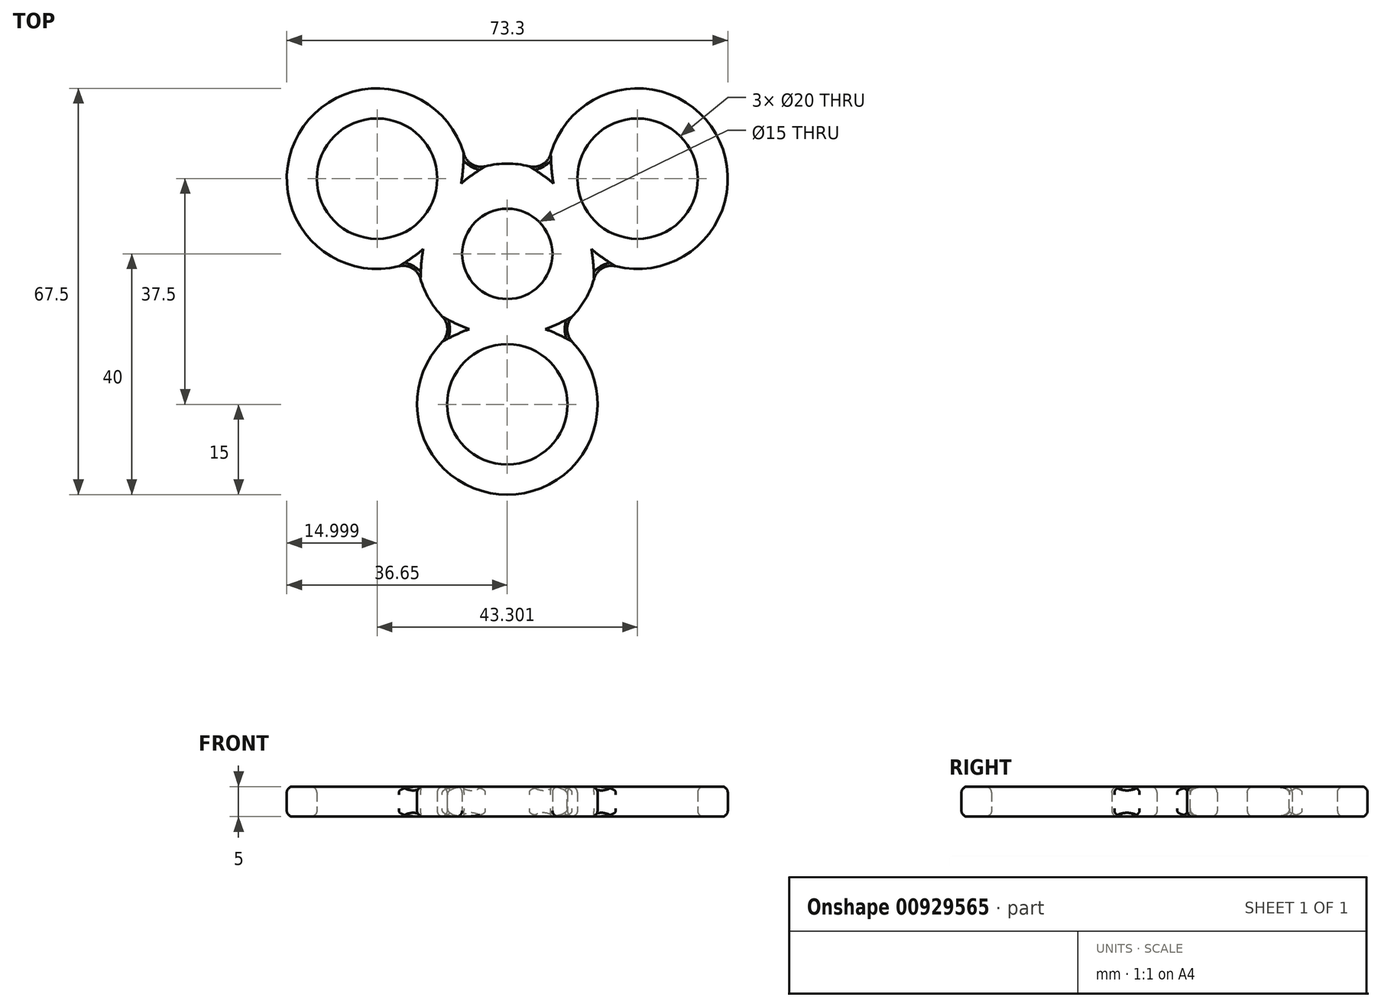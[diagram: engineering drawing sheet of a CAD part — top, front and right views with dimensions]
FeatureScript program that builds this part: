
annotation { "Feature Type Name" : "Feature", "Feature Type Description" : "" }
export const myFeature = defineFeature(function(context is Context, id is Id, definition is map)
    precondition{}
    {
        {
            var Q0;
            Q0=qCreatedBy(makeId("Top.planeOp"),FACE);
            var sketch = newSketch(context, id + "F0", { "sketchPlane" : qUnion([Q0])});
            skCircle(sketch, "E0", {"center": v(0, 0) * mm, "radius": 7.5 * mm});
            skCircle(sketch, "E1", {"center": v(0, 0) * mm, "radius": 15 * mm});
            skCircle(sketch, "E2", {"center": v(0, 0) * mm, "radius": 25 * mm, "construction": true});
            skLineSegment(sketch, "E3", {"start": v(0, 0) * mm, "end": v(0, -25) * mm, "construction": true});
            skCircle(sketch, "E4", {"center": v(0, -25) * mm, "radius": 15 * mm});
            skCircle(sketch, "E5", {"center": v(0, -25) * mm, "radius": 10 * mm});
            skCircle(sketch, "E6.1.0", {"center": v(21.65, 12.5) * mm, "radius": 15 * mm});
            skCircle(sketch, "E6.1.1", {"center": v(21.65, 12.5) * mm, "radius": 10 * mm});
            skCircle(sketch, "E6.2.0", {"center": v(-21.65, 12.5) * mm, "radius": 15 * mm});
            skCircle(sketch, "E6.2.1", {"center": v(-21.65, 12.5) * mm, "radius": 10 * mm});
            skSolve(sketch);
        }
        {
            var Q0;
            Q0 = qSketchRegion(id + "F0", true);
            extrude(context, id + "F1", {"entities" : qUnion([Q0]), "depth" : 5 * mm, "offsetDistance" : 25.4 * mm});
        }
        {
            var Q0;
            Q0=makeQuery(id+"F1.opExtrude","CAP_EDGE",EDGE,{"disambiguationData":[OSD([sQuery(id+"F0.wireOp",EDGE,"E6.2.0")])],"isStart":false});
            var Q1;
            Q1=makeQuery(id+"F1.opExtrude","CAP_EDGE",EDGE,{"disambiguationData":[OSD([sQuery(id+"F0.wireOp",EDGE,"E6.2.1")])],"isStart":false});
            var Q2;
            Q2=makeQuery(id+"F1.opExtrude","CAP_EDGE",EDGE,{"disambiguationData":[OSD([sQuery(id+"F0.wireOp",EDGE,"E6.2.1")])],"isStart":true});
            var Q3;
            Q3=makeQuery(id+"F1.opExtrude","CAP_EDGE",EDGE,{"disambiguationData":[OSD([sQuery(id+"F0.wireOp",EDGE,"E6.2.0")])],"isStart":true});
            var Q4;
            Q4=makeQuery(id+"F1.opExtrude","CAP_EDGE",EDGE,{"disambiguationData":[OSD([sQuery(id+"F0.wireOp",EDGE,"E0")])],"isStart":false});
            var Q5;
            Q5=makeQuery(id+"F1.opExtrude","CAP_EDGE",EDGE,{"disambiguationData":[OSD([sQuery(id+"F0.wireOp",EDGE,"E0")])],"isStart":true});
            var Q6;
            {var subQ0=sQuery(id+"F0.wireOp",EDGE,"E1");Q6=makeQuery(id+"F1.opExtrude","CAP_EDGE",EDGE,{"disambiguationData":[OSD([subQ0]),TDD([makeQuery(id+"F0.imprint","IMPRINT",EDGE,{"disambiguationData":[TD([[makeQuery(id+"F0.imprint","INTERSECT",VERTEX,{"disambiguationData":[OD(1.0)],"derivedFrom":[subQ0,sQuery(id+"F0.wireOp",EDGE,"E6.2.0")]}),-1.0]])],"derivedFrom":subQ0})])],"isStart":true});}
            var Q7;
            {var subQ0=sQuery(id+"F0.wireOp",EDGE,"E1");Q7=makeQuery(id+"F1.opExtrude","CAP_EDGE",EDGE,{"disambiguationData":[OSD([subQ0]),TDD([makeQuery(id+"F0.imprint","IMPRINT",EDGE,{"disambiguationData":[TD([[makeQuery(id+"F0.imprint","INTERSECT",VERTEX,{"disambiguationData":[OD(1.0)],"derivedFrom":[subQ0,sQuery(id+"F0.wireOp",EDGE,"E6.2.0")]}),-1.0]])],"derivedFrom":subQ0})])],"isStart":false});}
            var Q8;
            Q8=makeQuery(id+"F1.opExtrude","CAP_EDGE",EDGE,{"disambiguationData":[OSD([sQuery(id+"F0.wireOp",EDGE,"E4")])],"isStart":false});
            var Q9;
            Q9=makeQuery(id+"F1.opExtrude","CAP_EDGE",EDGE,{"disambiguationData":[OSD([sQuery(id+"F0.wireOp",EDGE,"E5")])],"isStart":false});
            var Q10;
            Q10=makeQuery(id+"F1.opExtrude","CAP_EDGE",EDGE,{"disambiguationData":[OSD([sQuery(id+"F0.wireOp",EDGE,"E5")])],"isStart":true});
            var Q11;
            Q11=makeQuery(id+"F1.opExtrude","CAP_EDGE",EDGE,{"disambiguationData":[OSD([sQuery(id+"F0.wireOp",EDGE,"E4")])],"isStart":true});
            var Q12;
            {var subQ0=sQuery(id+"F0.wireOp",EDGE,"E1");Q12=makeQuery(id+"F1.opExtrude","CAP_EDGE",EDGE,{"disambiguationData":[OSD([subQ0]),TDD([makeQuery(id+"F0.imprint","IMPRINT",EDGE,{"disambiguationData":[TD([[makeQuery(id+"F0.imprint","INTERSECT",VERTEX,{"disambiguationData":[OD(1.0)],"derivedFrom":[subQ0,sQuery(id+"F0.wireOp",EDGE,"E4")]}),-1.0]])],"derivedFrom":subQ0})])],"isStart":false});}
            var Q13;
            {var subQ0=sQuery(id+"F0.wireOp",EDGE,"E1");Q13=makeQuery(id+"F1.opExtrude","CAP_EDGE",EDGE,{"disambiguationData":[OSD([subQ0]),TDD([makeQuery(id+"F0.imprint","IMPRINT",EDGE,{"disambiguationData":[TD([[makeQuery(id+"F0.imprint","INTERSECT",VERTEX,{"disambiguationData":[OD(1.0)],"derivedFrom":[subQ0,sQuery(id+"F0.wireOp",EDGE,"E4")]}),-1.0]])],"derivedFrom":subQ0})])],"isStart":true});}
            var Q14;
            {var subQ0=sQuery(id+"F0.wireOp",EDGE,"E1");Q14=makeQuery(id+"F1.opExtrude","CAP_EDGE",EDGE,{"disambiguationData":[OSD([subQ0]),TDD([makeQuery(id+"F0.imprint","IMPRINT",EDGE,{"disambiguationData":[TD([[makeQuery(id+"F0.imprint","INTERSECT",VERTEX,{"disambiguationData":[OD(0.0)],"derivedFrom":[subQ0,sQuery(id+"F0.wireOp",EDGE,"E6.1.0")]}),-1.0]])],"derivedFrom":subQ0})])],"isStart":false});}
            var Q15;
            Q15=makeQuery(id+"F1.opExtrude","CAP_EDGE",EDGE,{"disambiguationData":[OSD([sQuery(id+"F0.wireOp",EDGE,"E6.1.1")])],"isStart":false});
            var Q16;
            Q16=makeQuery(id+"F1.opExtrude","CAP_EDGE",EDGE,{"disambiguationData":[OSD([sQuery(id+"F0.wireOp",EDGE,"E6.1.0")])],"isStart":false});
            var Q17;
            Q17=makeQuery(id+"F1.opExtrude","CAP_EDGE",EDGE,{"disambiguationData":[OSD([sQuery(id+"F0.wireOp",EDGE,"E6.1.1")])],"isStart":true});
            var Q18;
            Q18=makeQuery(id+"F1.opExtrude","CAP_EDGE",EDGE,{"disambiguationData":[OSD([sQuery(id+"F0.wireOp",EDGE,"E6.1.0")])],"isStart":true});
            var Q19;
            {var subQ0=sQuery(id+"F0.wireOp",EDGE,"E1");Q19=makeQuery(id+"F1.opExtrude","CAP_EDGE",EDGE,{"disambiguationData":[OSD([subQ0]),TDD([makeQuery(id+"F0.imprint","IMPRINT",EDGE,{"disambiguationData":[TD([[makeQuery(id+"F0.imprint","INTERSECT",VERTEX,{"disambiguationData":[OD(0.0)],"derivedFrom":[subQ0,sQuery(id+"F0.wireOp",EDGE,"E6.1.0")]}),-1.0]])],"derivedFrom":subQ0})])],"isStart":true});}
            fillet(context, id + "F2", {"entities" : qUnion([Q0, Q1, Q2, Q3, Q4, Q5, Q6, Q7, Q8, Q9, Q10, Q11, Q12, Q13, Q14, Q15, Q16, Q17, Q18, Q19]), "radius" : 1 * mm, "tangentPropagation" : true, "allowEdgeOverflow" : false});
        }
        {
            var Q0;
            {var subQ0=sQuery(id+"F0.wireOp",EDGE,"E4");var subQ1=sQuery(id+"F0.wireOp",EDGE,"E1");Q0=makeQuery(id+"F2.opFillet","BLEND_EDGE",EDGE,{"blendedFrom":[makeQuery(id+"F1.opExtrude","CAP_EDGE",EDGE,{"disambiguationData":[OSD([subQ1]),TDD([makeQuery(id+"F0.imprint","IMPRINT",EDGE,{"disambiguationData":[TD([[makeQuery(id+"F0.imprint","INTERSECT",VERTEX,{"disambiguationData":[OD(1.0)],"derivedFrom":[subQ1,subQ0]}),-1.0]])],"derivedFrom":subQ1})])],"isStart":false}),makeQuery(id+"F1.opExtrude","CAP_EDGE",EDGE,{"disambiguationData":[OSD([subQ0])],"isStart":false})],"blendedInto":[]});}
            var Q1;
            {var subQ0=sQuery(id+"F0.wireOp",EDGE,"E4");var subQ1=sQuery(id+"F0.wireOp",EDGE,"E1");Q1=makeQuery(id+"F2.opFillet","BLEND_EDGE",EDGE,{"blendedFrom":[makeQuery(id+"F1.opExtrude","CAP_EDGE",EDGE,{"disambiguationData":[OSD([subQ1]),TDD([makeQuery(id+"F0.imprint","IMPRINT",EDGE,{"disambiguationData":[TD([[makeQuery(id+"F0.imprint","INTERSECT",VERTEX,{"disambiguationData":[OD(1.0)],"derivedFrom":[subQ1,subQ0]}),-1.0]])],"derivedFrom":subQ1})])],"isStart":true}),makeQuery(id+"F1.opExtrude","CAP_EDGE",EDGE,{"disambiguationData":[OSD([subQ0])],"isStart":true})],"blendedInto":[]});}
            var Q2;
            {var subQ0=sQuery(id+"F0.wireOp",EDGE,"E4");var subQ1=sQuery(id+"F0.wireOp",EDGE,"E1");Q2=makeQuery(id+"F1.opExtrude","SWEPT_EDGE",EDGE,{"disambiguationData":[OSD([subQ1,subQ0]),TDD([makeQuery(id+"F0.imprint","INTERSECT",VERTEX,{"disambiguationData":[OD(1.0)],"derivedFrom":[subQ1,subQ0]})])]});}
            var Q3;
            {var subQ0=sQuery(id+"F0.wireOp",EDGE,"E6.1.0");var subQ1=sQuery(id+"F0.wireOp",EDGE,"E1");Q3=makeQuery(id+"F2.opFillet","BLEND_EDGE",EDGE,{"blendedFrom":[makeQuery(id+"F1.opExtrude","CAP_EDGE",EDGE,{"disambiguationData":[OSD([subQ1]),TDD([makeQuery(id+"F0.imprint","IMPRINT",EDGE,{"disambiguationData":[TD([[makeQuery(id+"F0.imprint","INTERSECT",VERTEX,{"disambiguationData":[OD(1.0)],"derivedFrom":[subQ1,sQuery(id+"F0.wireOp",EDGE,"E4")]}),-1.0]])],"derivedFrom":subQ1})])],"isStart":false}),makeQuery(id+"F1.opExtrude","CAP_EDGE",EDGE,{"disambiguationData":[OSD([subQ0])],"isStart":false})],"blendedInto":[]});}
            var Q4;
            {var subQ0=sQuery(id+"F0.wireOp",EDGE,"E6.1.0");var subQ1=sQuery(id+"F0.wireOp",EDGE,"E1");Q4=makeQuery(id+"F1.opExtrude","SWEPT_EDGE",EDGE,{"disambiguationData":[OSD([subQ1,subQ0]),TDD([makeQuery(id+"F0.imprint","INTERSECT",VERTEX,{"disambiguationData":[OD(1.0)],"derivedFrom":[subQ1,subQ0]})])]});}
            var Q5;
            {var subQ0=sQuery(id+"F0.wireOp",EDGE,"E6.1.0");var subQ1=sQuery(id+"F0.wireOp",EDGE,"E1");Q5=makeQuery(id+"F2.opFillet","BLEND_EDGE",EDGE,{"blendedFrom":[makeQuery(id+"F1.opExtrude","CAP_EDGE",EDGE,{"disambiguationData":[OSD([subQ1]),TDD([makeQuery(id+"F0.imprint","IMPRINT",EDGE,{"disambiguationData":[TD([[makeQuery(id+"F0.imprint","INTERSECT",VERTEX,{"disambiguationData":[OD(1.0)],"derivedFrom":[subQ1,sQuery(id+"F0.wireOp",EDGE,"E4")]}),-1.0]])],"derivedFrom":subQ1})])],"isStart":true}),makeQuery(id+"F1.opExtrude","CAP_EDGE",EDGE,{"disambiguationData":[OSD([subQ0])],"isStart":true})],"blendedInto":[]});}
            var Q6;
            {var subQ0=sQuery(id+"F0.wireOp",EDGE,"E6.1.0");var subQ1=sQuery(id+"F0.wireOp",EDGE,"E1");Q6=makeQuery(id+"F2.opFillet","BLEND_EDGE",EDGE,{"blendedFrom":[makeQuery(id+"F1.opExtrude","CAP_EDGE",EDGE,{"disambiguationData":[OSD([subQ1]),TDD([makeQuery(id+"F0.imprint","IMPRINT",EDGE,{"disambiguationData":[TD([[makeQuery(id+"F0.imprint","INTERSECT",VERTEX,{"disambiguationData":[OD(0.0)],"derivedFrom":[subQ1,subQ0]}),-1.0]])],"derivedFrom":subQ1})])],"isStart":false}),makeQuery(id+"F1.opExtrude","CAP_EDGE",EDGE,{"disambiguationData":[OSD([subQ0])],"isStart":false})],"blendedInto":[]});}
            var Q7;
            {var subQ0=sQuery(id+"F0.wireOp",EDGE,"E6.1.0");var subQ1=sQuery(id+"F0.wireOp",EDGE,"E1");Q7=makeQuery(id+"F1.opExtrude","SWEPT_EDGE",EDGE,{"disambiguationData":[OSD([subQ1,subQ0]),TDD([makeQuery(id+"F0.imprint","INTERSECT",VERTEX,{"disambiguationData":[OD(0.0)],"derivedFrom":[subQ1,subQ0]})])]});}
            var Q8;
            {var subQ0=sQuery(id+"F0.wireOp",EDGE,"E6.1.0");var subQ1=sQuery(id+"F0.wireOp",EDGE,"E1");Q8=makeQuery(id+"F2.opFillet","BLEND_EDGE",EDGE,{"blendedFrom":[makeQuery(id+"F1.opExtrude","CAP_EDGE",EDGE,{"disambiguationData":[OSD([subQ1]),TDD([makeQuery(id+"F0.imprint","IMPRINT",EDGE,{"disambiguationData":[TD([[makeQuery(id+"F0.imprint","INTERSECT",VERTEX,{"disambiguationData":[OD(0.0)],"derivedFrom":[subQ1,subQ0]}),-1.0]])],"derivedFrom":subQ1})])],"isStart":true}),makeQuery(id+"F1.opExtrude","CAP_EDGE",EDGE,{"disambiguationData":[OSD([subQ0])],"isStart":true})],"blendedInto":[]});}
            var Q9;
            {var subQ0=sQuery(id+"F0.wireOp",EDGE,"E6.2.0");var subQ1=sQuery(id+"F0.wireOp",EDGE,"E1");Q9=makeQuery(id+"F2.opFillet","BLEND_EDGE",EDGE,{"blendedFrom":[makeQuery(id+"F1.opExtrude","CAP_EDGE",EDGE,{"disambiguationData":[OSD([subQ1]),TDD([makeQuery(id+"F0.imprint","IMPRINT",EDGE,{"disambiguationData":[TD([[makeQuery(id+"F0.imprint","INTERSECT",VERTEX,{"disambiguationData":[OD(0.0)],"derivedFrom":[subQ1,sQuery(id+"F0.wireOp",EDGE,"E6.1.0")]}),-1.0]])],"derivedFrom":subQ1})])],"isStart":false}),makeQuery(id+"F1.opExtrude","CAP_EDGE",EDGE,{"disambiguationData":[OSD([subQ0])],"isStart":false})],"blendedInto":[]});}
            var Q10;
            {var subQ0=sQuery(id+"F0.wireOp",EDGE,"E6.2.0");var subQ1=sQuery(id+"F0.wireOp",EDGE,"E1");Q10=makeQuery(id+"F1.opExtrude","SWEPT_EDGE",EDGE,{"disambiguationData":[OSD([subQ1,subQ0]),TDD([makeQuery(id+"F0.imprint","INTERSECT",VERTEX,{"disambiguationData":[OD(0.0)],"derivedFrom":[subQ1,subQ0]})])]});}
            var Q11;
            {var subQ0=sQuery(id+"F0.wireOp",EDGE,"E6.2.0");var subQ1=sQuery(id+"F0.wireOp",EDGE,"E1");Q11=makeQuery(id+"F2.opFillet","BLEND_EDGE",EDGE,{"blendedFrom":[makeQuery(id+"F1.opExtrude","CAP_EDGE",EDGE,{"disambiguationData":[OSD([subQ1]),TDD([makeQuery(id+"F0.imprint","IMPRINT",EDGE,{"disambiguationData":[TD([[makeQuery(id+"F0.imprint","INTERSECT",VERTEX,{"disambiguationData":[OD(0.0)],"derivedFrom":[subQ1,sQuery(id+"F0.wireOp",EDGE,"E6.1.0")]}),-1.0]])],"derivedFrom":subQ1})])],"isStart":true}),makeQuery(id+"F1.opExtrude","CAP_EDGE",EDGE,{"disambiguationData":[OSD([subQ0])],"isStart":true})],"blendedInto":[]});}
            var Q12;
            {var subQ0=sQuery(id+"F0.wireOp",EDGE,"E6.2.0");var subQ1=sQuery(id+"F0.wireOp",EDGE,"E1");Q12=makeQuery(id+"F2.opFillet","BLEND_EDGE",EDGE,{"blendedFrom":[makeQuery(id+"F1.opExtrude","CAP_EDGE",EDGE,{"disambiguationData":[OSD([subQ1]),TDD([makeQuery(id+"F0.imprint","IMPRINT",EDGE,{"disambiguationData":[TD([[makeQuery(id+"F0.imprint","INTERSECT",VERTEX,{"disambiguationData":[OD(1.0)],"derivedFrom":[subQ1,subQ0]}),-1.0]])],"derivedFrom":subQ1})])],"isStart":false}),makeQuery(id+"F1.opExtrude","CAP_EDGE",EDGE,{"disambiguationData":[OSD([subQ0])],"isStart":false})],"blendedInto":[]});}
            var Q13;
            {var subQ0=sQuery(id+"F0.wireOp",EDGE,"E6.2.0");var subQ1=sQuery(id+"F0.wireOp",EDGE,"E1");Q13=makeQuery(id+"F1.opExtrude","SWEPT_EDGE",EDGE,{"disambiguationData":[OSD([subQ1,subQ0]),TDD([makeQuery(id+"F0.imprint","INTERSECT",VERTEX,{"disambiguationData":[OD(1.0)],"derivedFrom":[subQ1,subQ0]})])]});}
            var Q14;
            {var subQ0=sQuery(id+"F0.wireOp",EDGE,"E6.2.0");var subQ1=sQuery(id+"F0.wireOp",EDGE,"E1");Q14=makeQuery(id+"F2.opFillet","BLEND_EDGE",EDGE,{"blendedFrom":[makeQuery(id+"F1.opExtrude","CAP_EDGE",EDGE,{"disambiguationData":[OSD([subQ1]),TDD([makeQuery(id+"F0.imprint","IMPRINT",EDGE,{"disambiguationData":[TD([[makeQuery(id+"F0.imprint","INTERSECT",VERTEX,{"disambiguationData":[OD(1.0)],"derivedFrom":[subQ1,subQ0]}),-1.0]])],"derivedFrom":subQ1})])],"isStart":true}),makeQuery(id+"F1.opExtrude","CAP_EDGE",EDGE,{"disambiguationData":[OSD([subQ0])],"isStart":true})],"blendedInto":[]});}
            var Q15;
            {var subQ0=sQuery(id+"F0.wireOp",EDGE,"E4");var subQ1=sQuery(id+"F0.wireOp",EDGE,"E1");Q15=makeQuery(id+"F2.opFillet","BLEND_EDGE",EDGE,{"blendedFrom":[makeQuery(id+"F1.opExtrude","CAP_EDGE",EDGE,{"disambiguationData":[OSD([subQ1]),TDD([makeQuery(id+"F0.imprint","IMPRINT",EDGE,{"disambiguationData":[TD([[makeQuery(id+"F0.imprint","INTERSECT",VERTEX,{"disambiguationData":[OD(1.0)],"derivedFrom":[subQ1,sQuery(id+"F0.wireOp",EDGE,"E6.2.0")]}),-1.0]])],"derivedFrom":subQ1})])],"isStart":false}),makeQuery(id+"F1.opExtrude","CAP_EDGE",EDGE,{"disambiguationData":[OSD([subQ0])],"isStart":false})],"blendedInto":[]});}
            var Q16;
            {var subQ0=sQuery(id+"F0.wireOp",EDGE,"E4");var subQ1=sQuery(id+"F0.wireOp",EDGE,"E1");Q16=makeQuery(id+"F1.opExtrude","SWEPT_EDGE",EDGE,{"disambiguationData":[OSD([subQ1,subQ0]),TDD([makeQuery(id+"F0.imprint","INTERSECT",VERTEX,{"disambiguationData":[OD(0.0)],"derivedFrom":[subQ1,subQ0]})])]});}
            var Q17;
            {var subQ0=sQuery(id+"F0.wireOp",EDGE,"E4");var subQ1=sQuery(id+"F0.wireOp",EDGE,"E1");Q17=makeQuery(id+"F2.opFillet","BLEND_EDGE",EDGE,{"blendedFrom":[makeQuery(id+"F1.opExtrude","CAP_EDGE",EDGE,{"disambiguationData":[OSD([subQ1]),TDD([makeQuery(id+"F0.imprint","IMPRINT",EDGE,{"disambiguationData":[TD([[makeQuery(id+"F0.imprint","INTERSECT",VERTEX,{"disambiguationData":[OD(1.0)],"derivedFrom":[subQ1,sQuery(id+"F0.wireOp",EDGE,"E6.2.0")]}),-1.0]])],"derivedFrom":subQ1})])],"isStart":true}),makeQuery(id+"F1.opExtrude","CAP_EDGE",EDGE,{"disambiguationData":[OSD([subQ0])],"isStart":true})],"blendedInto":[]});}
            fillet(context, id + "F3", {"entities" : qUnion([Q0, Q1, Q2, Q3, Q4, Q5, Q6, Q7, Q8, Q9, Q10, Q11, Q12, Q13, Q14, Q15, Q16, Q17]), "radius" : 3 * mm, "tangentPropagation" : true, "allowEdgeOverflow" : false});
        }
    });
